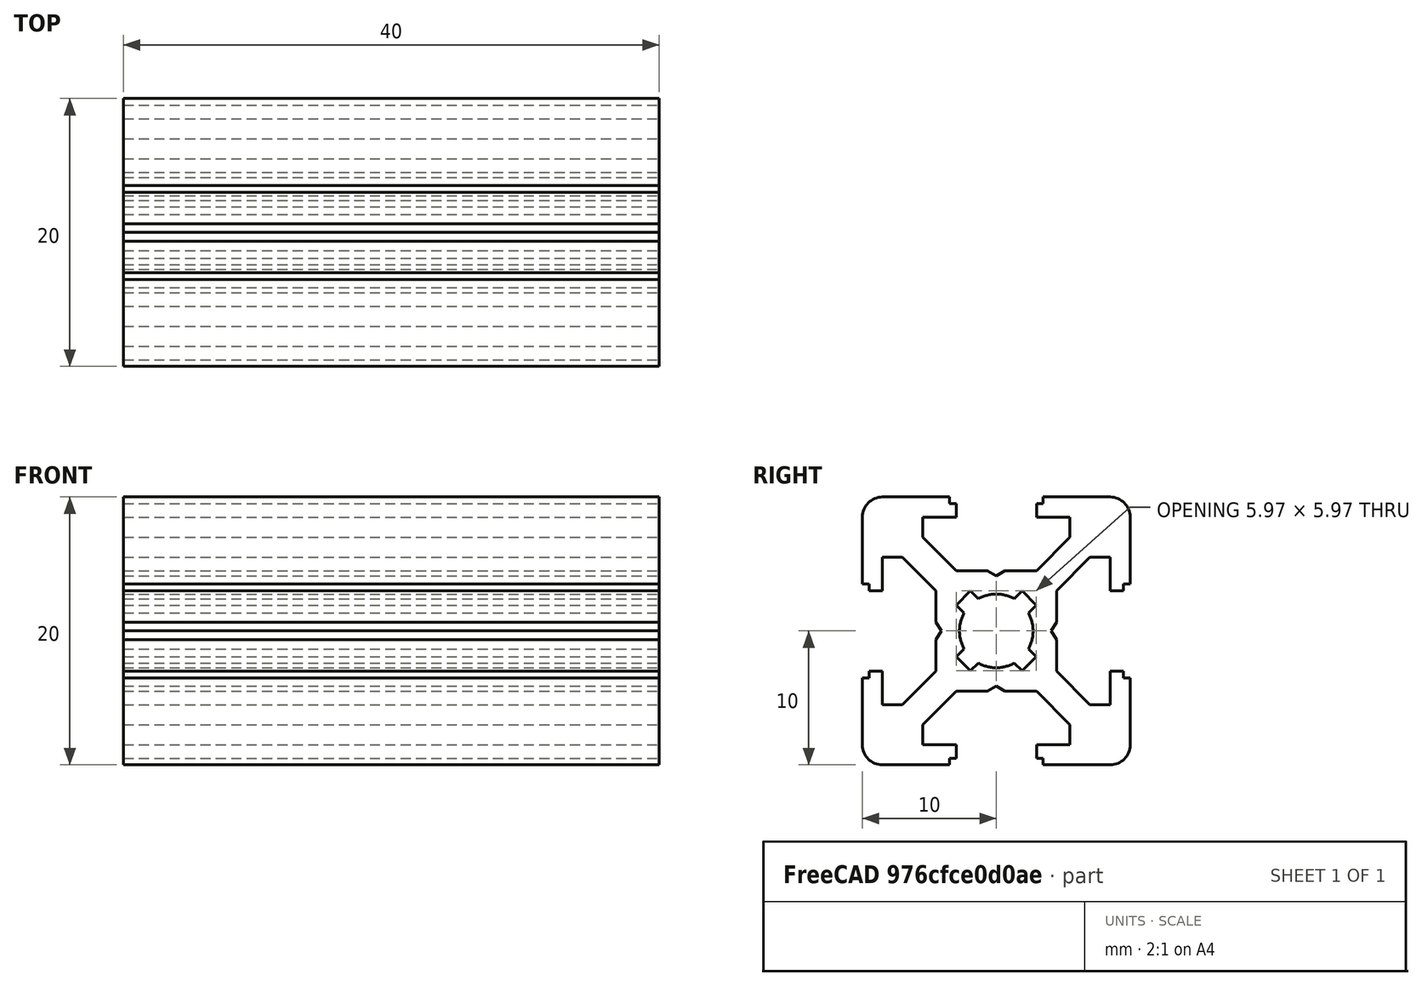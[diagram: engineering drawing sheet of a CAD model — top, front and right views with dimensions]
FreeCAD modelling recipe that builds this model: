
FCSTD DOCUMENT  (FreeCAD 0.19R)
Label: Tslot4
License: All rights reserved
LicenseURL: http://en.wikipedia.org/wiki/All_rights_reserved
objects: Sketcher::SketchObject×1, PartDesign::Pad×1, PartDesign::Body×1
note: 4 computed .brp shape members not serialized (recipe doc carries the construction recipe); baked Part::Feature solids carry a one-line shape summary decoded from their .brp

FEATURE [Sketcher::SketchObject] Sketch  label="T-Slot-Skizze"
  FullyConstrained = true
  MapMode = 5
  Placement = pos=(0,0,0) rot=(0.57735,0.57735,0.57735;2.0944rad)
  Support = -> [YZ_Plane]
  sketch-geometry (98):
    g0: LineSegment StartX=0 StartY=4.1 StartZ=0 EndX=0.65 EndY=4.5 EndZ=0
    g1: LineSegment StartX=0.65 StartY=4.5 StartZ=0 EndX=3 EndY=4.5 EndZ=0
    g2: LineSegment StartX=3 StartY=4.5 StartZ=0 EndX=5.5 EndY=7 EndZ=0
    g3: LineSegment StartX=5.5 StartY=7 StartZ=0 EndX=5.5 EndY=8.5 EndZ=0
    g4: LineSegment StartX=5.5 StartY=8.5 StartZ=0 EndX=3 EndY=8.5 EndZ=0
    g5: LineSegment StartX=3 StartY=8.5 StartZ=0 EndX=3 EndY=9.5 EndZ=0
    g6: LineSegment StartX=3 StartY=9.5 StartZ=0 EndX=3.5 EndY=9.5 EndZ=0
    g7: LineSegment StartX=3.5 StartY=9.5 StartZ=0 EndX=3.5 EndY=10 EndZ=0
    g8: LineSegment StartX=3.5 StartY=10 StartZ=0 EndX=8.5 EndY=10 EndZ=0
    g9: LineSegment StartX=10 StartY=8.5 StartZ=0 EndX=10 EndY=3.5 EndZ=0
    g10: LineSegment StartX=10 StartY=3.5 StartZ=0 EndX=9.5 EndY=3.5 EndZ=0
    g11: LineSegment StartX=9.5 StartY=3.5 StartZ=0 EndX=9.5 EndY=3 EndZ=0
    g12: LineSegment StartX=9.5 StartY=3 StartZ=0 EndX=8.5 EndY=3 EndZ=0
    g13: LineSegment StartX=8.5 StartY=3 StartZ=0 EndX=8.5 EndY=5.5 EndZ=0
    g14: LineSegment StartX=8.5 StartY=5.5 StartZ=0 EndX=7 EndY=5.5 EndZ=0
    g15: LineSegment StartX=7 StartY=5.5 StartZ=0 EndX=4.5 EndY=3 EndZ=0
    g16: LineSegment StartX=4.5 StartY=3 StartZ=0 EndX=4.5 EndY=0.65 EndZ=0
    g17: LineSegment StartX=4.5 StartY=0.65 StartZ=0 EndX=4.1 EndY=0 EndZ=0
    g18: ArcOfCircle CenterX=8.5 CenterY=8.5 CenterZ=0 NormalX=0 NormalY=0 NormalZ=1 AngleXU=0 Radius=1.5 StartAngle=0 EndAngle=1.5708
    g19: LineSegment StartX=0 StartY=-4.1 StartZ=0 EndX=0.65 EndY=-4.5 EndZ=0
    g20: LineSegment StartX=0.65 StartY=-4.5 StartZ=0 EndX=3 EndY=-4.5 EndZ=0
    g21: LineSegment StartX=3 StartY=-4.5 StartZ=0 EndX=5.5 EndY=-7 EndZ=0
    g22: LineSegment StartX=5.5 StartY=-7 StartZ=0 EndX=5.5 EndY=-8.5 EndZ=0
    g23: LineSegment StartX=5.5 StartY=-8.5 StartZ=0 EndX=3 EndY=-8.5 EndZ=0
    g24: LineSegment StartX=3 StartY=-8.5 StartZ=0 EndX=3 EndY=-9.5 EndZ=0
    g25: LineSegment StartX=3 StartY=-9.5 StartZ=0 EndX=3.5 EndY=-9.5 EndZ=0
    g26: LineSegment StartX=3.5 StartY=-9.5 StartZ=0 EndX=3.5 EndY=-10 EndZ=0
    g27: LineSegment StartX=3.5 StartY=-10 StartZ=0 EndX=8.5 EndY=-10 EndZ=0
    g28: LineSegment StartX=10 StartY=-8.5 StartZ=0 EndX=10 EndY=-3.5 EndZ=0
    g29: LineSegment StartX=10 StartY=-3.5 StartZ=0 EndX=9.5 EndY=-3.5 EndZ=0
    g30: LineSegment StartX=9.5 StartY=-3.5 StartZ=0 EndX=9.5 EndY=-3 EndZ=0
    g31: LineSegment StartX=9.5 StartY=-3 StartZ=0 EndX=8.5 EndY=-3 EndZ=0
    g32: LineSegment StartX=8.5 StartY=-3 StartZ=0 EndX=8.5 EndY=-5.5 EndZ=0
    g33: LineSegment StartX=8.5 StartY=-5.5 StartZ=0 EndX=7 EndY=-5.5 EndZ=0
    g34: LineSegment StartX=7 StartY=-5.5 StartZ=0 EndX=4.5 EndY=-3 EndZ=0
    g35: LineSegment StartX=4.5 StartY=-3 StartZ=0 EndX=4.5 EndY=-0.65 EndZ=0
    g36: ArcOfCircle CenterX=8.5 CenterY=-8.5 CenterZ=0 NormalX=0 NormalY=0 NormalZ=1 AngleXU=0 Radius=1.5 StartAngle=4.71239 EndAngle=6.28319
    g37: LineSegment StartX=4.5 StartY=-0.65 StartZ=0 EndX=4.1 EndY=0 EndZ=0
    g38: LineSegment StartX=0 StartY=-4.1 StartZ=0 EndX=-0.65 EndY=-4.5 EndZ=0
    g39: LineSegment StartX=-0.65 StartY=-4.5 StartZ=0 EndX=-3 EndY=-4.5 EndZ=0
    g40: LineSegment StartX=-3 StartY=-4.5 StartZ=0 EndX=-5.5 EndY=-7 EndZ=0
    g41: LineSegment StartX=-5.5 StartY=-7 StartZ=0 EndX=-5.5 EndY=-8.5 EndZ=0
    g42: LineSegment StartX=-5.5 StartY=-8.5 StartZ=0 EndX=-3 EndY=-8.5 EndZ=0
    g43: LineSegment StartX=-3 StartY=-8.5 StartZ=0 EndX=-3 EndY=-9.5 EndZ=0
    g44: LineSegment StartX=-3 StartY=-9.5 StartZ=0 EndX=-3.5 EndY=-9.5 EndZ=0
    g45: LineSegment StartX=-3.5 StartY=-9.5 StartZ=0 EndX=-3.5 EndY=-10 EndZ=0
    g46: LineSegment StartX=-3.5 StartY=-10 StartZ=0 EndX=-8.5 EndY=-10 EndZ=0
    g47: LineSegment StartX=-10 StartY=-8.5 StartZ=0 EndX=-10 EndY=-3.5 EndZ=0
    g48: LineSegment StartX=-10 StartY=-3.5 StartZ=0 EndX=-9.5 EndY=-3.5 EndZ=0
    g49: LineSegment StartX=-9.5 StartY=-3.5 StartZ=0 EndX=-9.5 EndY=-3 EndZ=0
    g50: LineSegment StartX=-9.5 StartY=-3 StartZ=0 EndX=-8.5 EndY=-3 EndZ=0
    g51: LineSegment StartX=-8.5 StartY=-3 StartZ=0 EndX=-8.5 EndY=-5.5 EndZ=0
    g52: LineSegment StartX=-8.5 StartY=-5.5 StartZ=0 EndX=-7 EndY=-5.5 EndZ=0
    g53: LineSegment StartX=-7 StartY=-5.5 StartZ=0 EndX=-4.5 EndY=-3 EndZ=0
    g54: LineSegment StartX=-4.5 StartY=-3 StartZ=0 EndX=-4.5 EndY=-0.65 EndZ=0
    g55: ArcOfCircle CenterX=-8.5 CenterY=-8.5 CenterZ=0 NormalX=0 NormalY=0 NormalZ=1 AngleXU=0 Radius=1.5 StartAngle=3.14159 EndAngle=4.71239
    g56: LineSegment StartX=-4.5 StartY=-0.65 StartZ=0 EndX=-4.1 EndY=0 EndZ=0
    g57: LineSegment StartX=-0.65 StartY=4.5 StartZ=0 EndX=-3 EndY=4.5 EndZ=0
    g58: LineSegment StartX=-3 StartY=4.5 StartZ=0 EndX=-5.5 EndY=7 EndZ=0
    g59: LineSegment StartX=-5.5 StartY=7 StartZ=0 EndX=-5.5 EndY=8.5 EndZ=0
    g60: LineSegment StartX=-5.5 StartY=8.5 StartZ=0 EndX=-3 EndY=8.5 EndZ=0
    g61: LineSegment StartX=-3 StartY=8.5 StartZ=0 EndX=-3 EndY=9.5 EndZ=0
    g62: LineSegment StartX=-3 StartY=9.5 StartZ=0 EndX=-3.5 EndY=9.5 EndZ=0
    g63: LineSegment StartX=-3.5 StartY=9.5 StartZ=0 EndX=-3.5 EndY=10 EndZ=0
    g64: LineSegment StartX=-3.5 StartY=10 StartZ=0 EndX=-8.5 EndY=10 EndZ=0
    g65: LineSegment StartX=-10 StartY=8.5 StartZ=0 EndX=-10 EndY=3.5 EndZ=0
    g66: LineSegment StartX=-10 StartY=3.5 StartZ=0 EndX=-9.5 EndY=3.5 EndZ=0
    g67: LineSegment StartX=-9.5 StartY=3.5 StartZ=0 EndX=-9.5 EndY=3 EndZ=0
    g68: LineSegment StartX=-9.5 StartY=3 StartZ=0 EndX=-8.5 EndY=3 EndZ=0
    g69: LineSegment StartX=-8.5 StartY=3 StartZ=0 EndX=-8.5 EndY=5.5 EndZ=0
    g70: LineSegment StartX=-8.5 StartY=5.5 StartZ=0 EndX=-7 EndY=5.5 EndZ=0
    g71: LineSegment StartX=-7 StartY=5.5 StartZ=0 EndX=-4.5 EndY=3 EndZ=0
    g72: LineSegment StartX=-4.5 StartY=3 StartZ=0 EndX=-4.5 EndY=0.65 EndZ=0
    g73: ArcOfCircle CenterX=-8.5 CenterY=8.5 CenterZ=0 NormalX=0 NormalY=0 NormalZ=1 AngleXU=0 Radius=1.5 StartAngle=1.5708 EndAngle=3.14159
    g74: LineSegment StartX=-4.5 StartY=0.65 StartZ=0 EndX=-4.1 EndY=0 EndZ=0
    g75: LineSegment StartX=0 StartY=4.1 StartZ=0 EndX=-0.65 EndY=4.5 EndZ=0
    g76: Circle CenterX=0 CenterY=0 CenterZ=0 NormalX=0 NormalY=0 NormalZ=1 AngleXU=0 Radius=3.55
    g77: Circle CenterX=0 CenterY=0 CenterZ=0 NormalX=0 NormalY=0 NormalZ=1 AngleXU=0 Radius=2.75
    g78: LineSegment StartX=1.3405 StartY=2.40116 StartZ=0 EndX=1.92324 EndY=2.9839 EndZ=0
    g79: LineSegment StartX=1.92324 StartY=2.9839 StartZ=0 EndX=2.9839 EndY=1.92324 EndZ=0
    g80: LineSegment StartX=2.9839 StartY=1.92324 StartZ=0 EndX=2.40116 EndY=1.3405 EndZ=0
    g81: ArcOfCircle CenterX=0 CenterY=0 CenterZ=0 NormalX=0 NormalY=0 NormalZ=1 AngleXU=0 Radius=2.75 StartAngle=0 EndAngle=0.509172
    g82: ArcOfCircle CenterX=0 CenterY=0 CenterZ=0 NormalX=0 NormalY=0 NormalZ=1 AngleXU=0 Radius=2.75 StartAngle=1.06162 EndAngle=1.5708
    g83: LineSegment StartX=-1.3405 StartY=2.40116 StartZ=0 EndX=-1.92324 EndY=2.9839 EndZ=0
    g84: LineSegment StartX=-1.92324 StartY=2.9839 StartZ=0 EndX=-2.9839 EndY=1.92324 EndZ=0
    g85: LineSegment StartX=-2.9839 StartY=1.92324 StartZ=0 EndX=-2.40116 EndY=1.3405 EndZ=0
    g86: ArcOfCircle CenterX=-1.3e-15 CenterY=6e-16 CenterZ=0 NormalX=0 NormalY=0 NormalZ=1 AngleXU=0 Radius=2.75 StartAngle=2.63242 EndAngle=3.14159
    g87: ArcOfCircle CenterX=-1.3e-15 CenterY=6e-16 CenterZ=0 NormalX=0 NormalY=0 NormalZ=1 AngleXU=0 Radius=2.75 StartAngle=1.5708 EndAngle=2.07997
    g88: LineSegment StartX=-1.34051 StartY=-2.40115 StartZ=0 EndX=-1.92325 EndY=-2.98389 EndZ=0
    g89: LineSegment StartX=-1.92325 StartY=-2.98389 StartZ=0 EndX=-2.9839 EndY=-1.92323 EndZ=0
    g90: LineSegment StartX=-2.9839 StartY=-1.92323 StartZ=0 EndX=-2.40116 EndY=-1.34049 EndZ=0
    g91: ArcOfCircle CenterX=-3e-16 CenterY=2e-16 CenterZ=0 NormalX=0 NormalY=0 NormalZ=1 AngleXU=0 Radius=2.75 StartAngle=3.14159 EndAngle=3.65076
    g92: ArcOfCircle CenterX=-3e-16 CenterY=2e-16 CenterZ=0 NormalX=0 NormalY=0 NormalZ=1 AngleXU=0 Radius=2.75 StartAngle=4.20321 EndAngle=4.71239
    g93: LineSegment StartX=1.34051 StartY=-2.40115 StartZ=0 EndX=1.92325 EndY=-2.98389 EndZ=0
    g94: LineSegment StartX=1.92325 StartY=-2.98389 StartZ=0 EndX=2.9839 EndY=-1.92323 EndZ=0
    g95: LineSegment StartX=2.9839 StartY=-1.92323 StartZ=0 EndX=2.40116 EndY=-1.34049 EndZ=0
    g96: ArcOfCircle CenterX=3e-16 CenterY=2e-16 CenterZ=0 NormalX=0 NormalY=0 NormalZ=1 AngleXU=0 Radius=2.75 StartAngle=4.71239 EndAngle=5.22156
    g97: ArcOfCircle CenterX=3e-16 CenterY=2e-16 CenterZ=0 NormalX=0 NormalY=0 NormalZ=1 AngleXU=0 Radius=2.75 StartAngle=5.77402 EndAngle=6.28319
  constraints (291):
    c: PointOnObject(g0,g-2)
    c: Coincident(g0,g1)
    c: Horizontal(g1)
    c: Coincident(g1,g2)
    c: Coincident(g2,g3)
    c: Vertical(g3)
    c: Coincident(g3,g4)
    c: Horizontal(g4)
    c: Coincident(g4,g5)
    c: Vertical(g5)
    c: Coincident(g5,g6)
    c: Horizontal(g6)
    c: Coincident(g6,g7)
    c: Coincident(g7,g8)
    c: Horizontal(g8)
    c: Vertical(g7)
    c: DistanceX(g-1,g5) = 3
    c: DistanceY(g4,g7) = 1.5
    c: DistanceY(g0,g7) = 5.5
    c: DistanceY(g3,g3) = 1.5
    c: DistanceY(g4,g5) = 1
    c: DistanceX(g-1,g1) = 3
    c: DistanceX(g-1,g7) = 3.5
    c: DistanceX(g0,g0) = 0.65
    c: DistanceY(g0,g0) = 0.4
    c: DistanceX(g-1,g3) = 5.5
    c: Vertical(g9)
    c: Coincident(g9,g10)
    c: Coincident(g10,g11)
    c: Coincident(g11,g12)
    c: Coincident(g12,g13)
    c: Vertical(g13)
    c: Coincident(g13,g14)
    c: Horizontal(g14)
    c: Coincident(g14,g15)
    c: Coincident(g15,g16)
    c: Vertical(g16)
    c: Coincident(g16,g17)
    c: PointOnObject(g17,g-1)
    c: Horizontal(g10)
    c: Horizontal(g12)
    c: Vertical(g11)
    c: Equal(g17,g0)
    c: Equal(g1,g16)
    c: Equal(g15,g2)
    c: Equal(g3,g14)
    c: Equal(g13,g4)
    c: Equal(g12,g5)
    c: Parallel(g15,g2)
    c: Equal(g11,g6)
    c: Equal(g10,g7)
    c: Equal(g9,g8)
    c: Tangent(g8,g18) = 1.5708
    c: Tangent(g9,g18) = 1.5708
    c: Radius(g18) = 1.5
    c: DistanceY(g-1,g8) = 10
    c: DistanceX(g-1,g9) = 10
    c: Coincident(g19,g20)
    c: Horizontal(g20)
    c: Coincident(g20,g21)
    c: Coincident(g21,g22)
    c: Vertical(g22)
    c: Coincident(g22,g23)
    c: Horizontal(g23)
    c: Coincident(g23,g24)
    c: Vertical(g24)
    c: Coincident(g24,g25)
    c: Horizontal(g25)
    c: Coincident(g25,g26)
    c: Coincident(g26,g27)
    c: Horizontal(g27)
    c: Vertical(g26)
    c: Vertical(g28)
    c: Coincident(g28,g29)
    c: Coincident(g29,g30)
    c: Coincident(g30,g31)
    c: Coincident(g31,g32)
    c: Vertical(g32)
    c: Coincident(g32,g33)
    c: Horizontal(g33)
    c: Coincident(g33,g34)
    c: Coincident(g34,g35)
    c: Vertical(g35)
    c: Coincident(g35,g37)
    c: Horizontal(g29)
    c: Horizontal(g31)
    c: Vertical(g30)
    c: Equal(g37,g19)
    c: Equal(g20,g35)
    c: Equal(g34,g21)
    c: Equal(g22,g33)
    c: Equal(g32,g23)
    c: Equal(g31,g24)
    c: Parallel(g34,g21)
    c: Equal(g30,g25)
    c: Equal(g29,g26)
    c: Equal(g28,g27)
    c: Tangent(g27,g36) = -1.5708
    c: Tangent(g28,g36) = -1.5708
    c: Radius(g36) = 1.5
    c: Equal(g9,g28)
    c: Equal(g12,g31)
    c: DistanceX(g-1,g28) = 10
    c: DistanceY(g27,g-1) = 10
    c: DistanceY(g30,g-1) = 3
    c: Equal(g33,g14)
    c: Equal(g35,g16)
    c: Equal(g17,g37)
    c: Coincident(g37,g17)
    c: Equal(g15,g34)
    c: PointOnObject(g19,g-2)
    c: DistanceY(g34,g-1) = 3
    c: DistanceX(g-1,g20) = 3
    c: Coincident(g38,g39)
    c: Horizontal(g39)
    c: Coincident(g39,g40)
    c: Coincident(g40,g41)
    c: Vertical(g41)
    c: Coincident(g41,g42)
    c: Horizontal(g42)
    c: Coincident(g42,g43)
    c: Vertical(g43)
    c: Coincident(g43,g44)
    c: Horizontal(g44)
    c: Coincident(g44,g45)
    c: Coincident(g45,g46)
    c: Horizontal(g46)
    c: Vertical(g45)
    c: Vertical(g47)
    c: Coincident(g47,g48)
    c: Coincident(g48,g49)
    c: Coincident(g49,g50)
    c: Coincident(g50,g51)
    c: Vertical(g51)
    c: Coincident(g51,g52)
    c: Horizontal(g52)
    c: Coincident(g52,g53)
    c: Coincident(g53,g54)
    c: Vertical(g54)
    c: Coincident(g54,g56)
    c: Horizontal(g48)
    c: Horizontal(g50)
    c: Vertical(g49)
    c: Equal(g39,g54)
    c: Equal(g53,g40)
    c: Equal(g41,g52)
    c: Equal(g51,g42)
    c: Equal(g50,g43)
    c: Parallel(g53,g40)
    c: Equal(g49,g44)
    c: Equal(g48,g45)
    c: Equal(g47,g46)
    c: Tangent(g46,g55) = 1.5708
    c: Tangent(g47,g55) = 1.5708
    c: Radius(g55) = 1.5
    c: Coincident(g38,g19)
    c: DistanceX(g39,g-1) = 3
    c: DistanceX(g38,g19) = 0.65
    c: DistanceY(g38,g19) = 0.4
    c: PointOnObject(g56,g-1)
    c: Equal(g56,g38)
    c: DistanceY(g53,g-1) = 3
    c: Equal(g22,g41)
    c: Equal(g42,g23)
    c: Equal(g24,g43)
    c: Equal(g25,g44)
    c: Equal(g26,g45)
    c: DistanceY(g46,g-1) = 10
    c: DistanceX(g47,g-1) = 10
    c: Coincident(g75,g57)
    c: Horizontal(g57)
    c: Coincident(g57,g58)
    c: Coincident(g58,g59)
    c: Vertical(g59)
    c: Coincident(g59,g60)
    c: Horizontal(g60)
    c: Coincident(g60,g61)
    c: Vertical(g61)
    c: Coincident(g61,g62)
    c: Horizontal(g62)
    c: Coincident(g62,g63)
    c: Coincident(g63,g64)
    c: Horizontal(g64)
    c: Vertical(g63)
    c: Vertical(g65)
    c: Coincident(g65,g66)
    c: Coincident(g66,g67)
    c: Coincident(g67,g68)
    c: Coincident(g68,g69)
    c: Vertical(g69)
    c: Coincident(g69,g70)
    c: Horizontal(g70)
    c: Coincident(g70,g71)
    c: Coincident(g71,g72)
    c: Vertical(g72)
    c: Coincident(g72,g74)
    c: Horizontal(g66)
    c: Horizontal(g68)
    c: Vertical(g67)
    c: Equal(g57,g72)
    c: Equal(g71,g58)
    c: Equal(g59,g70)
    c: Equal(g69,g60)
    c: Equal(g68,g61)
    c: Parallel(g71,g58)
    c: Equal(g67,g62)
    c: Equal(g66,g63)
    c: Equal(g65,g64)
    c: Tangent(g64,g73) = -1.5708
    c: Tangent(g65,g73) = -1.5708
    c: Radius(g73) = 1.5
    c: Equal(g74,g75)
    c: Coincident(g56,g74)
    c: Coincident(g0,g75)
    c: Equal(g0,g75)
    c: Equal(g1,g57)
    c: Equal(g2,g58)
    c: Equal(g3,g59)
    c: Equal(g4,g60)
    c: Equal(g5,g61)
    c: Equal(g6,g62)
    c: Equal(g7,g63)
    c: Equal(g8,g64)
    c: DistanceX(g65,g-1) = 10
    c: Coincident(g76,g-1)
    c: Coincident(g77,g-1)
    c: Radius(g76) = 3.55
    c: Radius(g77) = 2.75
    c: PointOnObject(g78,g77)
    c: PointOnObject(g78,g76)
    c: Coincident(g78,g79)
    c: PointOnObject(g79,g76)
    c: Coincident(g79,g80)
    c: PointOnObject(g80,g77)
    c: Coincident(g81,g-1)
    c: Coincident(g81,g80)
    c: Coincident(g82,g81)
    c: Coincident(g82,g78)
    c: Parallel(g78,g80)
    c: Parallel(g78,g2)
    c: Distance(g79) = 1.5
    c: Distance(g78,g80) = 1.5
    c: PointOnObject(g82,g-2)
    c: PointOnObject(g81,g-1)
    c: Coincident(g83,g84)
    c: Coincident(g84,g85)
    c: Coincident(g86,g85)
    c: Coincident(g87,g86)
    c: Coincident(g87,g83)
    c: Parallel(g83,g85)
    c: Distance(g84) = 1.5
    c: Distance(g83,g85) = 1.5
    c: Coincident(g82,g87)
    c: PointOnObject(g86,g-1)
    c: PointOnObject(g83,g76)
    c: PointOnObject(g83,g77)
    c: PointOnObject(g85,g77)
    c: PointOnObject(g84,g76)
    c: PointOnObject(g86,g77)
    c: Parallel(g85,g71)
    c: Coincident(g88,g89)
    c: Coincident(g89,g90)
    c: Coincident(g91,g90)
    c: Coincident(g92,g91)
    c: Coincident(g92,g88)
    c: Parallel(g88,g90)
    c: Distance(g89) = 1.5
    c: Distance(g88,g90) = 1.5
    c: PointOnObject(g88,g77)
    c: PointOnObject(g90,g77)
    c: Coincident(g86,g91)
    c: PointOnObject(g89,g76)
    c: PointOnObject(g88,g76)
    c: PointOnObject(g92,g-2)
    c: PointOnObject(g92,g77)
    c: Parallel(g88,g40)
    c: Coincident(g93,g94)
    c: Coincident(g94,g95)
    c: Coincident(g97,g95)
    c: Coincident(g96,g97)
    c: Coincident(g96,g93)
    c: Parallel(g93,g95)
    c: Distance(g94) = 1.5
    c: Distance(g93,g95) = 1.5
    c: Coincident(g81,g97)
    c: Coincident(g92,g96)
    c: PointOnObject(g93,g77)
    c: PointOnObject(g95,g77)
    c: PointOnObject(g94,g76)
    c: PointOnObject(g93,g76)
    c: Parallel(g93,g21)
FEATURE [PartDesign::Pad] Pad  label="T-Slot-Element"
  Direction = (1,1,1)
  Length = 40
  Length2 = 100
  Placement = pos=(0,0,0) rot=(0.57735,0.57735,0.57735;2.0944rad)
  Profile = -> Sketch
  Type = 0
FEATURE [PartDesign::Body] Body  label="T-Slot-Profil 20x20"
  Group = -> [Sketch,Pad]
  Origin = -> Origin
  Tip = -> Pad
